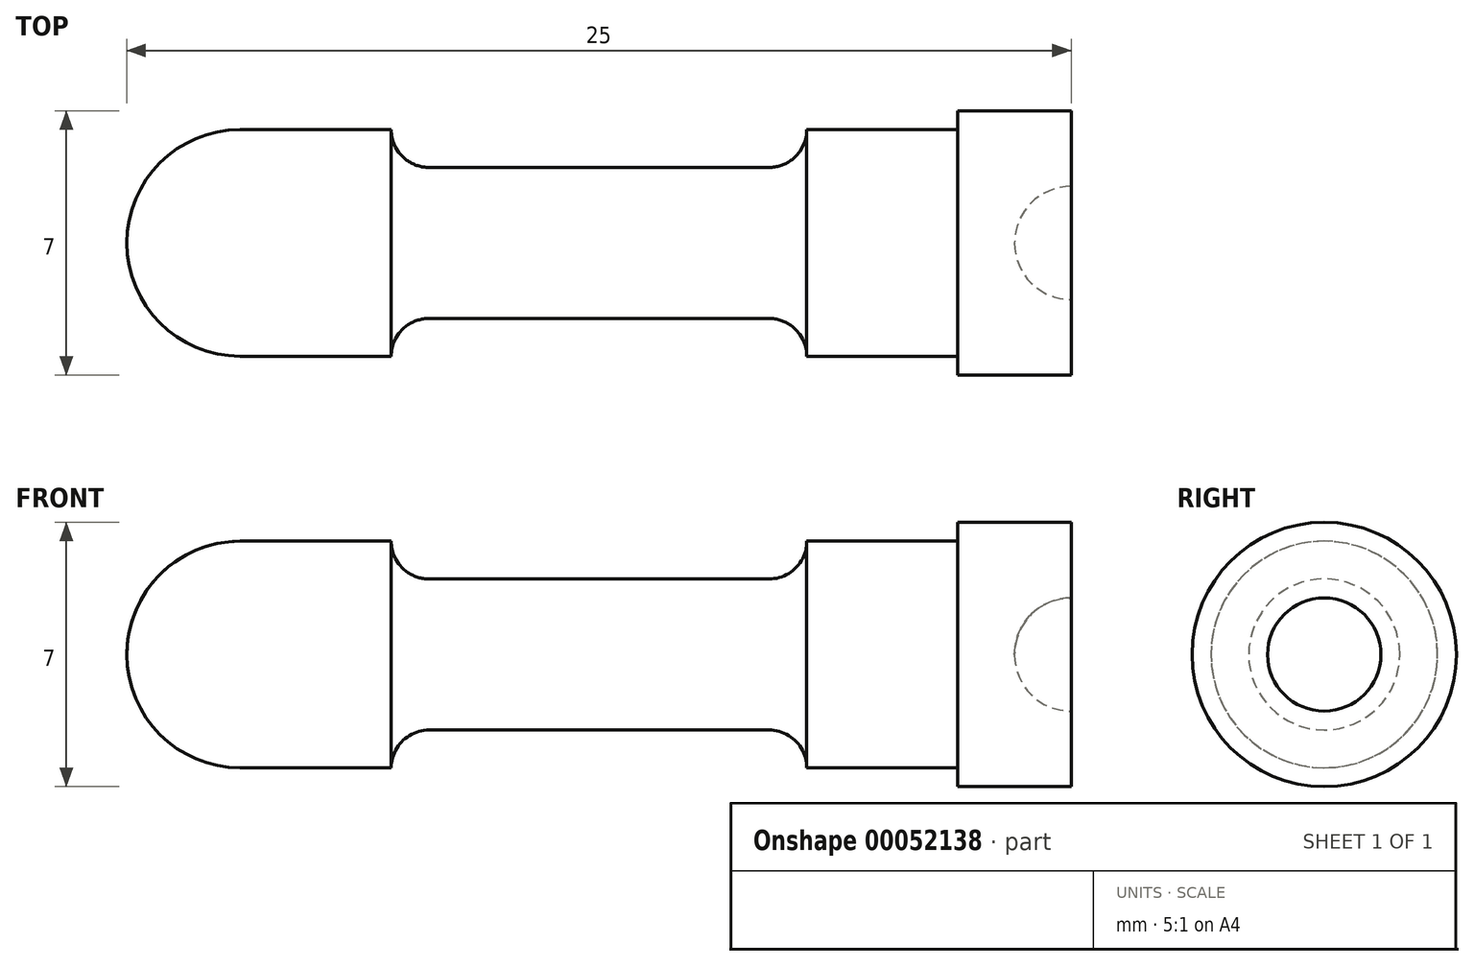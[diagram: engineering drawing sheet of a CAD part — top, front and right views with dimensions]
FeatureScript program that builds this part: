
annotation { "Feature Type Name" : "Feature", "Feature Type Description" : "" }
export const myFeature = defineFeature(function(context is Context, id is Id, definition is map)
    precondition{}
    {
        {
            var Q0;
            Q0=qCreatedBy(makeId("Front.planeOp"),FACE);
            var sketch = newSketch(context, id + "F0", { "sketchPlane" : qUnion([Q0])});
            skArc(sketch, "E0", {"start": v(0, 3) * mm, "mid": v(-2.12, 2.12) * mm, "end": v(-3, 0) * mm});
            skLineSegment(sketch, "E1", {"start": v(0, 3) * mm, "end": v(4, 3) * mm});
            skLineSegment(sketch, "E2", {"start": v(4, 3) * mm, "end": v(4, 3) * mm});
            skLineSegment(sketch, "E3", {"start": v(5, 2) * mm, "end": v(14, 2) * mm});
            skLineSegment(sketch, "E4", {"start": v(15, 3) * mm, "end": v(15, 3) * mm});
            skLineSegment(sketch, "E5", {"start": v(15, 3) * mm, "end": v(19, 3) * mm});
            skLineSegment(sketch, "E6", {"start": v(19, 3) * mm, "end": v(19, 3.5) * mm});
            skLineSegment(sketch, "E7", {"start": v(19, 3.5) * mm, "end": v(22, 3.5) * mm});
            skLineSegment(sketch, "E8", {"start": v(22, 3.5) * mm, "end": v(22, 1.5) * mm});
            skArc(sketch, "E9", {"start": v(22, 1.5) * mm, "mid": v(20.94, 1.06) * mm, "end": v(20.5, 0) * mm});
            skLineSegment(sketch, "E10.MirrorCS", {"start": v(4, -3) * mm, "end": v(4, -3) * mm});
            skLineSegment(sketch, "E11.MirrorCS", {"start": v(15, -3) * mm, "end": v(15, -3) * mm});
            skPoint(sketch, "E12.visualSharp", {"position": v(4, 2) * mm});
            skArc(sketch, "E12.filletArc", {"start": v(4, 3) * mm, "mid": v(4.3, 2.3) * mm, "end": v(5, 2) * mm});
            skPoint(sketch, "E13.visualSharp", {"position": v(4, -2) * mm});
            skPoint(sketch, "E14.visualSharp", {"position": v(15, -2) * mm});
            skPoint(sketch, "E15.visualSharp", {"position": v(15, 2) * mm});
            skArc(sketch, "E15.filletArc", {"start": v(14, 2) * mm, "mid": v(14.7, 2.3) * mm, "end": v(15, 3) * mm});
            skLineSegment(sketch, "E16", {"start": v(20.5, 0) * mm, "end": v(-3, 0) * mm});
            skPoint(sketch, "E17.MirrorCS.end.orphan", {"position": v(4, -3) * mm});
            skPoint(sketch, "E17.MirrorCS.start.orphan", {"position": v(0, -3) * mm});
            skPoint(sketch, "E18.MirrorCS.end.orphan", {"position": v(19, -3) * mm});
            skPoint(sketch, "E18.MirrorCS.start.orphan", {"position": v(15, -3) * mm});
            skPoint(sketch, "E19.MirrorCS.end.orphan", {"position": v(22, -3.5) * mm});
            skPoint(sketch, "E19.MirrorCS.start.orphan", {"position": v(19, -3.5) * mm});
            skSolve(sketch);
        }
        {
            var Q0;
            Q0=makeQuery(id+"F0.imprint","IMPRINT",FACE,{"disambiguationData":[TD([[makeQuery(id+"F0.imprint","IMPRINT",EDGE,{"derivedFrom":sQuery(id+"F0.wireOp",EDGE,"E0")}),1.0]])]});
            var Q1;
            Q1=sQuery(id+"F0.wireOp",EDGE,"E16");
            revolve(context, id + "F1", {"entities" : qUnion([Q0]), "axis" : qUnion([Q1]), "revolveType" : RevolveType.FULL});
        }
    });
